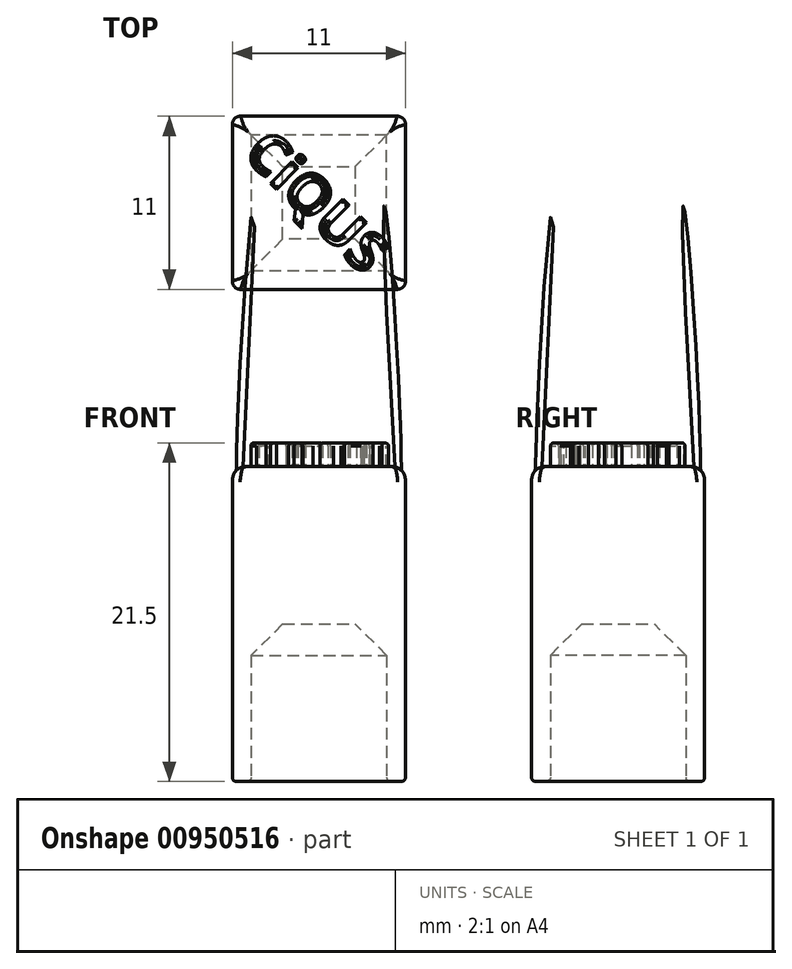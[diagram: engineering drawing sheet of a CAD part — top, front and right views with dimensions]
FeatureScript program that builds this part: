
annotation { "Feature Type Name" : "Feature", "Feature Type Description" : "" }
export const myFeature = defineFeature(function(context is Context, id is Id, definition is map)
    precondition{}
    {
        {
            var Q0;
            Q0=qCreatedBy(makeId("Top.planeOp"),FACE);
            var sketch = newSketch(context, id + "F0", { "sketchPlane" : qUnion([Q0])});
            skLineSegment(sketch, "E0.bottom", {"start": v(5.5, -5.5) * mm, "end": v(-5.5, -5.5) * mm});
            skLineSegment(sketch, "E0.top", {"start": v(5.5, 5.5) * mm, "end": v(-5.5, 5.5) * mm});
            skLineSegment(sketch, "E0.left", {"start": v(5.5, -5.5) * mm, "end": v(5.5, 5.5) * mm});
            skLineSegment(sketch, "E0.right", {"start": v(-5.5, -5.5) * mm, "end": v(-5.5, 5.5) * mm});
            skPoint(sketch, "E0.middle", {"position": v(0, 0) * mm});
            skSolve(sketch);
        }
        {
            var Q0;
            Q0=makeQuery(id+"F0.imprint","IMPRINT",FACE,{"disambiguationData":[TD([[makeQuery(id+"F0.imprint","IMPRINT",EDGE,{"derivedFrom":sQuery(id+"F0.wireOp",EDGE,"E0.bottom")}),-1.0]])]});
            extrude(context, id + "F1", {"entities" : qUnion([Q0]), "depth" : 20 * mm, "offsetDistance" : 25 * mm});
        }
        {
            var Q0;
            Q0=makeQuery(id+"F1.opExtrude","CAP_FACE",FACE,{"disambiguationData":[OSD([sQuery(id+"F0.wireOp",EDGE,"E0.bottom"),sQuery(id+"F0.wireOp",EDGE,"E0.top"),sQuery(id+"F0.wireOp",EDGE,"E0.left"),sQuery(id+"F0.wireOp",EDGE,"E0.right")])],"isStart":true});
            var sketch = newSketch(context, id + "F2", { "sketchPlane" : qUnion([Q0])});
            skLineSegment(sketch, "E1.bottom", {"start": v(-4.3, 4.3) * mm, "end": v(4.3, 4.3) * mm});
            skLineSegment(sketch, "E1.top", {"start": v(-4.3, -4.3) * mm, "end": v(4.3, -4.3) * mm});
            skLineSegment(sketch, "E1.left", {"start": v(-4.3, 4.3) * mm, "end": v(-4.3, -4.3) * mm});
            skLineSegment(sketch, "E1.right", {"start": v(4.3, 4.3) * mm, "end": v(4.3, -4.3) * mm});
            skPoint(sketch, "E1.middle", {"position": v(0, 0) * mm});
            skSolve(sketch);
        }
        {
            var Q0;
            Q0 = qSketchRegion(id + "F2", true);
            extrude(context, id + "F3", {"entities" : qUnion([Q0]), "operationType" : NewBodyOperationType.REMOVE, "oppositeDirection" : true, "depth" : 10 * mm, "offsetDistance" : 25 * mm});
        }
        {
            var Q0;
            Q0=makeQuery(id+"F1.opExtrude","CAP_FACE",FACE,{"disambiguationData":[OSD([sQuery(id+"F0.wireOp",EDGE,"E0.bottom"),sQuery(id+"F0.wireOp",EDGE,"E0.top"),sQuery(id+"F0.wireOp",EDGE,"E0.left"),sQuery(id+"F0.wireOp",EDGE,"E0.right")])],"isStart":true});
            fillet(context, id + "F4", {"entities" : qUnion([Q0]), "radius" : .25 * mm, "tangentPropagation" : true, "allowEdgeOverflow" : false});
        }
        {
            var Q0;
            Q0=makeQuery(id+"F3.boolean.opBoolean","COPY",FACE,{"derivedFrom":makeQuery(id+"F3.opExtrude","CAP_FACE",FACE,{"disambiguationData":[OSD([sQuery(id+"F2.wireOp",EDGE,"E1.bottom"),sQuery(id+"F2.wireOp",EDGE,"E1.top"),sQuery(id+"F2.wireOp",EDGE,"E1.left"),sQuery(id+"F2.wireOp",EDGE,"E1.right")])],"isStart":false})});
            chamfer(context, id + "F5", {"entities" : qUnion([Q0]), "width" : 2 * mm, "tangentPropagation" : true});
        }
        {
            var Q0;
            Q0=makeQuery(id+"F1.opExtrude","CAP_FACE",FACE,{"disambiguationData":[OSD([sQuery(id+"F0.wireOp",EDGE,"E0.bottom"),sQuery(id+"F0.wireOp",EDGE,"E0.top"),sQuery(id+"F0.wireOp",EDGE,"E0.left"),sQuery(id+"F0.wireOp",EDGE,"E0.right")])],"isStart":false});
            var sketch = newSketch(context, id + "F6", { "sketchPlane" : qUnion([Q0])});
            skText(sketch, "E2", { "text": "CiQUS", "fontName": "OpenSans-Bold.ttf"});
            const initialGuessF6  = {"E2": [-0.0055, -0.00258, 1, 0, 0.00258]};
            skSetInitialGuess(sketch, initialGuessF6);
            skSolve(sketch);
        }
        {
            var Q0;
            Q0 = qSketchRegion(id + "F6", true);
            extrude(context, id + "F7", {"entities" : qUnion([Q0]), "depth" : 1.5 * mm, "offsetDistance" : 25 * mm});
        }
        {
            var Q0;
            Q0=makeQuery(id+"F7.opExtrude","SWEPT_BODY",BODY,{"disambiguationData":[OSD([sQuery(id+"F6.wireOp",EDGE,"E2.sketch_text.stroke-0"),sQuery(id+"F6.wireOp",EDGE,"E2.sketch_text.stroke-1"),sQuery(id+"F6.wireOp",EDGE,"E2.sketch_text.stroke-2"),sQuery(id+"F6.wireOp",EDGE,"E2.sketch_text.stroke-3"),sQuery(id+"F6.wireOp",EDGE,"E2.sketch_text.stroke-4"),sQuery(id+"F6.wireOp",EDGE,"E2.sketch_text.stroke-5"),sQuery(id+"F6.wireOp",EDGE,"E2.sketch_text.stroke-6"),sQuery(id+"F6.wireOp",EDGE,"E2.sketch_text.stroke-7"),sQuery(id+"F6.wireOp",EDGE,"E2.sketch_text.stroke-8"),sQuery(id+"F6.wireOp",EDGE,"E2.sketch_text.stroke-9"),sQuery(id+"F6.wireOp",EDGE,"E2.sketch_text.stroke-10"),sQuery(id+"F6.wireOp",EDGE,"E2.sketch_text.stroke-11"),sQuery(id+"F6.wireOp",EDGE,"E2.sketch_text.stroke-12"),sQuery(id+"F6.wireOp",EDGE,"E2.sketch_text.stroke-13"),sQuery(id+"F6.wireOp",EDGE,"E2.sketch_text.stroke-14")])]});
            var Q1;
            Q1=makeQuery(id+"F7.opExtrude","SWEPT_BODY",BODY,{"disambiguationData":[OSD([sQuery(id+"F6.wireOp",EDGE,"E2.sketch_text.stroke-15"),sQuery(id+"F6.wireOp",EDGE,"E2.sketch_text.stroke-16"),sQuery(id+"F6.wireOp",EDGE,"E2.sketch_text.stroke-17"),sQuery(id+"F6.wireOp",EDGE,"E2.sketch_text.stroke-18"),sQuery(id+"F6.wireOp",EDGE,"E2.sketch_text.stroke-19")])]});
            var Q2;
            Q2=makeQuery(id+"F7.opExtrude","SWEPT_BODY",BODY,{"disambiguationData":[OSD([sQuery(id+"F6.wireOp",EDGE,"E2.sketch_text.stroke-20"),sQuery(id+"F6.wireOp",EDGE,"E2.sketch_text.stroke-21"),sQuery(id+"F6.wireOp",EDGE,"E2.sketch_text.stroke-22"),sQuery(id+"F6.wireOp",EDGE,"E2.sketch_text.stroke-23")])]});
            var Q3;
            Q3=makeQuery(id+"F7.opExtrude","SWEPT_BODY",BODY,{"disambiguationData":[OSD([sQuery(id+"F6.wireOp",EDGE,"E2.sketch_text.stroke-24"),sQuery(id+"F6.wireOp",EDGE,"E2.sketch_text.stroke-25"),sQuery(id+"F6.wireOp",EDGE,"E2.sketch_text.stroke-26"),sQuery(id+"F6.wireOp",EDGE,"E2.sketch_text.stroke-27"),sQuery(id+"F6.wireOp",EDGE,"E2.sketch_text.stroke-28"),sQuery(id+"F6.wireOp",EDGE,"E2.sketch_text.stroke-29"),sQuery(id+"F6.wireOp",EDGE,"E2.sketch_text.stroke-30"),sQuery(id+"F6.wireOp",EDGE,"E2.sketch_text.stroke-31"),sQuery(id+"F6.wireOp",EDGE,"E2.sketch_text.stroke-32"),sQuery(id+"F6.wireOp",EDGE,"E2.sketch_text.stroke-33"),sQuery(id+"F6.wireOp",EDGE,"E2.sketch_text.stroke-34"),sQuery(id+"F6.wireOp",EDGE,"E2.sketch_text.stroke-35"),sQuery(id+"F6.wireOp",EDGE,"E2.sketch_text.stroke-36"),sQuery(id+"F6.wireOp",EDGE,"E2.sketch_text.stroke-37"),sQuery(id+"F6.wireOp",EDGE,"E2.sketch_text.stroke-38"),sQuery(id+"F6.wireOp",EDGE,"E2.sketch_text.stroke-39"),sQuery(id+"F6.wireOp",EDGE,"E2.sketch_text.stroke-40"),sQuery(id+"F6.wireOp",EDGE,"E2.sketch_text.stroke-41")])]});
            var Q4;
            Q4=makeQuery(id+"F7.opExtrude","SWEPT_BODY",BODY,{"disambiguationData":[OSD([sQuery(id+"F6.wireOp",EDGE,"E2.sketch_text.stroke-42"),sQuery(id+"F6.wireOp",EDGE,"E2.sketch_text.stroke-43"),sQuery(id+"F6.wireOp",EDGE,"E2.sketch_text.stroke-44"),sQuery(id+"F6.wireOp",EDGE,"E2.sketch_text.stroke-45"),sQuery(id+"F6.wireOp",EDGE,"E2.sketch_text.stroke-46"),sQuery(id+"F6.wireOp",EDGE,"E2.sketch_text.stroke-47"),sQuery(id+"F6.wireOp",EDGE,"E2.sketch_text.stroke-48"),sQuery(id+"F6.wireOp",EDGE,"E2.sketch_text.stroke-49"),sQuery(id+"F6.wireOp",EDGE,"E2.sketch_text.stroke-50"),sQuery(id+"F6.wireOp",EDGE,"E2.sketch_text.stroke-51"),sQuery(id+"F6.wireOp",EDGE,"E2.sketch_text.stroke-52"),sQuery(id+"F6.wireOp",EDGE,"E2.sketch_text.stroke-53"),sQuery(id+"F6.wireOp",EDGE,"E2.sketch_text.stroke-54"),sQuery(id+"F6.wireOp",EDGE,"E2.sketch_text.stroke-55"),sQuery(id+"F6.wireOp",EDGE,"E2.sketch_text.stroke-56")])]});
            var Q5;
            Q5=makeQuery(id+"F7.opExtrude","SWEPT_BODY",BODY,{"disambiguationData":[OSD([sQuery(id+"F6.wireOp",EDGE,"E2.sketch_text.stroke-57"),sQuery(id+"F6.wireOp",EDGE,"E2.sketch_text.stroke-58"),sQuery(id+"F6.wireOp",EDGE,"E2.sketch_text.stroke-59"),sQuery(id+"F6.wireOp",EDGE,"E2.sketch_text.stroke-60"),sQuery(id+"F6.wireOp",EDGE,"E2.sketch_text.stroke-61"),sQuery(id+"F6.wireOp",EDGE,"E2.sketch_text.stroke-62"),sQuery(id+"F6.wireOp",EDGE,"E2.sketch_text.stroke-63"),sQuery(id+"F6.wireOp",EDGE,"E2.sketch_text.stroke-64"),sQuery(id+"F6.wireOp",EDGE,"E2.sketch_text.stroke-65"),sQuery(id+"F6.wireOp",EDGE,"E2.sketch_text.stroke-66"),sQuery(id+"F6.wireOp",EDGE,"E2.sketch_text.stroke-67"),sQuery(id+"F6.wireOp",EDGE,"E2.sketch_text.stroke-68"),sQuery(id+"F6.wireOp",EDGE,"E2.sketch_text.stroke-69"),sQuery(id+"F6.wireOp",EDGE,"E2.sketch_text.stroke-70"),sQuery(id+"F6.wireOp",EDGE,"E2.sketch_text.stroke-71"),sQuery(id+"F6.wireOp",EDGE,"E2.sketch_text.stroke-72"),sQuery(id+"F6.wireOp",EDGE,"E2.sketch_text.stroke-73"),sQuery(id+"F6.wireOp",EDGE,"E2.sketch_text.stroke-74"),sQuery(id+"F6.wireOp",EDGE,"E2.sketch_text.stroke-75"),sQuery(id+"F6.wireOp",EDGE,"E2.sketch_text.stroke-76"),sQuery(id+"F6.wireOp",EDGE,"E2.sketch_text.stroke-77"),sQuery(id+"F6.wireOp",EDGE,"E2.sketch_text.stroke-78"),sQuery(id+"F6.wireOp",EDGE,"E2.sketch_text.stroke-79"),sQuery(id+"F6.wireOp",EDGE,"E2.sketch_text.stroke-80"),sQuery(id+"F6.wireOp",EDGE,"E2.sketch_text.stroke-81"),sQuery(id+"F6.wireOp",EDGE,"E2.sketch_text.stroke-82"),sQuery(id+"F6.wireOp",EDGE,"E2.sketch_text.stroke-83"),sQuery(id+"F6.wireOp",EDGE,"E2.sketch_text.stroke-84")])]});
            var Q6;
            Q6=makeQuery(id+"F1.opExtrude","SWEPT_EDGE",EDGE,{"disambiguationData":[OSD([sQuery(id+"F0.wireOp",EDGE,"E0.bottom"),sQuery(id+"F0.wireOp",EDGE,"E0.left")])]});
            transform(context, id + "F8", {"entities" : qUnion([Q0, Q1, Q2, Q3, Q4, Q5]), "transformType" : TransformType.ROTATION, "transformAxis" : qUnion([Q6]), "angle" : 45 * degree, "makeCopy" : false});
        }
        {
            var Q0;
            Q0=makeQuery(id+"F7.opExtrude","SWEPT_BODY",BODY,{"disambiguationData":[OSD([sQuery(id+"F6.wireOp",EDGE,"E2.sketch_text.stroke-0"),sQuery(id+"F6.wireOp",EDGE,"E2.sketch_text.stroke-1"),sQuery(id+"F6.wireOp",EDGE,"E2.sketch_text.stroke-2"),sQuery(id+"F6.wireOp",EDGE,"E2.sketch_text.stroke-3"),sQuery(id+"F6.wireOp",EDGE,"E2.sketch_text.stroke-4"),sQuery(id+"F6.wireOp",EDGE,"E2.sketch_text.stroke-5"),sQuery(id+"F6.wireOp",EDGE,"E2.sketch_text.stroke-6"),sQuery(id+"F6.wireOp",EDGE,"E2.sketch_text.stroke-7"),sQuery(id+"F6.wireOp",EDGE,"E2.sketch_text.stroke-8"),sQuery(id+"F6.wireOp",EDGE,"E2.sketch_text.stroke-9"),sQuery(id+"F6.wireOp",EDGE,"E2.sketch_text.stroke-10"),sQuery(id+"F6.wireOp",EDGE,"E2.sketch_text.stroke-11"),sQuery(id+"F6.wireOp",EDGE,"E2.sketch_text.stroke-12"),sQuery(id+"F6.wireOp",EDGE,"E2.sketch_text.stroke-13"),sQuery(id+"F6.wireOp",EDGE,"E2.sketch_text.stroke-14")])]});
            var Q1;
            Q1=makeQuery(id+"F7.opExtrude","SWEPT_BODY",BODY,{"disambiguationData":[OSD([sQuery(id+"F6.wireOp",EDGE,"E2.sketch_text.stroke-15"),sQuery(id+"F6.wireOp",EDGE,"E2.sketch_text.stroke-16"),sQuery(id+"F6.wireOp",EDGE,"E2.sketch_text.stroke-17"),sQuery(id+"F6.wireOp",EDGE,"E2.sketch_text.stroke-18"),sQuery(id+"F6.wireOp",EDGE,"E2.sketch_text.stroke-19")])]});
            var Q2;
            Q2=makeQuery(id+"F7.opExtrude","SWEPT_BODY",BODY,{"disambiguationData":[OSD([sQuery(id+"F6.wireOp",EDGE,"E2.sketch_text.stroke-20"),sQuery(id+"F6.wireOp",EDGE,"E2.sketch_text.stroke-21"),sQuery(id+"F6.wireOp",EDGE,"E2.sketch_text.stroke-22"),sQuery(id+"F6.wireOp",EDGE,"E2.sketch_text.stroke-23")])]});
            var Q3;
            Q3=makeQuery(id+"F7.opExtrude","SWEPT_BODY",BODY,{"disambiguationData":[OSD([sQuery(id+"F6.wireOp",EDGE,"E2.sketch_text.stroke-24"),sQuery(id+"F6.wireOp",EDGE,"E2.sketch_text.stroke-25"),sQuery(id+"F6.wireOp",EDGE,"E2.sketch_text.stroke-26"),sQuery(id+"F6.wireOp",EDGE,"E2.sketch_text.stroke-27"),sQuery(id+"F6.wireOp",EDGE,"E2.sketch_text.stroke-28"),sQuery(id+"F6.wireOp",EDGE,"E2.sketch_text.stroke-29"),sQuery(id+"F6.wireOp",EDGE,"E2.sketch_text.stroke-30"),sQuery(id+"F6.wireOp",EDGE,"E2.sketch_text.stroke-31"),sQuery(id+"F6.wireOp",EDGE,"E2.sketch_text.stroke-32"),sQuery(id+"F6.wireOp",EDGE,"E2.sketch_text.stroke-33"),sQuery(id+"F6.wireOp",EDGE,"E2.sketch_text.stroke-34"),sQuery(id+"F6.wireOp",EDGE,"E2.sketch_text.stroke-35"),sQuery(id+"F6.wireOp",EDGE,"E2.sketch_text.stroke-36"),sQuery(id+"F6.wireOp",EDGE,"E2.sketch_text.stroke-37"),sQuery(id+"F6.wireOp",EDGE,"E2.sketch_text.stroke-38"),sQuery(id+"F6.wireOp",EDGE,"E2.sketch_text.stroke-39"),sQuery(id+"F6.wireOp",EDGE,"E2.sketch_text.stroke-40"),sQuery(id+"F6.wireOp",EDGE,"E2.sketch_text.stroke-41")])]});
            var Q4;
            Q4=makeQuery(id+"F7.opExtrude","SWEPT_BODY",BODY,{"disambiguationData":[OSD([sQuery(id+"F6.wireOp",EDGE,"E2.sketch_text.stroke-42"),sQuery(id+"F6.wireOp",EDGE,"E2.sketch_text.stroke-43"),sQuery(id+"F6.wireOp",EDGE,"E2.sketch_text.stroke-44"),sQuery(id+"F6.wireOp",EDGE,"E2.sketch_text.stroke-45"),sQuery(id+"F6.wireOp",EDGE,"E2.sketch_text.stroke-46"),sQuery(id+"F6.wireOp",EDGE,"E2.sketch_text.stroke-47"),sQuery(id+"F6.wireOp",EDGE,"E2.sketch_text.stroke-48"),sQuery(id+"F6.wireOp",EDGE,"E2.sketch_text.stroke-49"),sQuery(id+"F6.wireOp",EDGE,"E2.sketch_text.stroke-50"),sQuery(id+"F6.wireOp",EDGE,"E2.sketch_text.stroke-51"),sQuery(id+"F6.wireOp",EDGE,"E2.sketch_text.stroke-52"),sQuery(id+"F6.wireOp",EDGE,"E2.sketch_text.stroke-53"),sQuery(id+"F6.wireOp",EDGE,"E2.sketch_text.stroke-54"),sQuery(id+"F6.wireOp",EDGE,"E2.sketch_text.stroke-55"),sQuery(id+"F6.wireOp",EDGE,"E2.sketch_text.stroke-56")])]});
            var Q5;
            Q5=makeQuery(id+"F7.opExtrude","SWEPT_BODY",BODY,{"disambiguationData":[OSD([sQuery(id+"F6.wireOp",EDGE,"E2.sketch_text.stroke-57"),sQuery(id+"F6.wireOp",EDGE,"E2.sketch_text.stroke-58"),sQuery(id+"F6.wireOp",EDGE,"E2.sketch_text.stroke-59"),sQuery(id+"F6.wireOp",EDGE,"E2.sketch_text.stroke-60"),sQuery(id+"F6.wireOp",EDGE,"E2.sketch_text.stroke-61"),sQuery(id+"F6.wireOp",EDGE,"E2.sketch_text.stroke-62"),sQuery(id+"F6.wireOp",EDGE,"E2.sketch_text.stroke-63"),sQuery(id+"F6.wireOp",EDGE,"E2.sketch_text.stroke-64"),sQuery(id+"F6.wireOp",EDGE,"E2.sketch_text.stroke-65"),sQuery(id+"F6.wireOp",EDGE,"E2.sketch_text.stroke-66"),sQuery(id+"F6.wireOp",EDGE,"E2.sketch_text.stroke-67"),sQuery(id+"F6.wireOp",EDGE,"E2.sketch_text.stroke-68"),sQuery(id+"F6.wireOp",EDGE,"E2.sketch_text.stroke-69"),sQuery(id+"F6.wireOp",EDGE,"E2.sketch_text.stroke-70"),sQuery(id+"F6.wireOp",EDGE,"E2.sketch_text.stroke-71"),sQuery(id+"F6.wireOp",EDGE,"E2.sketch_text.stroke-72"),sQuery(id+"F6.wireOp",EDGE,"E2.sketch_text.stroke-73"),sQuery(id+"F6.wireOp",EDGE,"E2.sketch_text.stroke-74"),sQuery(id+"F6.wireOp",EDGE,"E2.sketch_text.stroke-75"),sQuery(id+"F6.wireOp",EDGE,"E2.sketch_text.stroke-76"),sQuery(id+"F6.wireOp",EDGE,"E2.sketch_text.stroke-77"),sQuery(id+"F6.wireOp",EDGE,"E2.sketch_text.stroke-78"),sQuery(id+"F6.wireOp",EDGE,"E2.sketch_text.stroke-79"),sQuery(id+"F6.wireOp",EDGE,"E2.sketch_text.stroke-80"),sQuery(id+"F6.wireOp",EDGE,"E2.sketch_text.stroke-81"),sQuery(id+"F6.wireOp",EDGE,"E2.sketch_text.stroke-82"),sQuery(id+"F6.wireOp",EDGE,"E2.sketch_text.stroke-83"),sQuery(id+"F6.wireOp",EDGE,"E2.sketch_text.stroke-84")])]});
            transform(context, id + "F9", {"entities" : qUnion([Q0, Q1, Q2, Q3, Q4, Q5]), "transformType" : TransformType.TRANSLATION_3D, "dx" : -4.68 * mm, "dy" : -1.3 * mm, "dz" : 0 * mm, "makeCopy" : false});
        }
        {
            var Q0;
            Q0=makeQuery(id+"F1.opExtrude","CAP_FACE",FACE,{"disambiguationData":[OSD([sQuery(id+"F0.wireOp",EDGE,"E0.bottom"),sQuery(id+"F0.wireOp",EDGE,"E0.top"),sQuery(id+"F0.wireOp",EDGE,"E0.left"),sQuery(id+"F0.wireOp",EDGE,"E0.right")])],"isStart":false});
            fillet(context, id + "F10", {"entities" : qUnion([Q0]), "radius" : 1 * mm, "tangentPropagation" : true, "rho" : 0.5, "crossSection" : FilletCrossSection.CONIC, "allowEdgeOverflow" : false});
        }
        {
            var Q0;
            Q0=makeQuery(id+"F1.opExtrude","SWEPT_EDGE",EDGE,{"disambiguationData":[OSD([sQuery(id+"F0.wireOp",EDGE,"E0.bottom"),sQuery(id+"F0.wireOp",EDGE,"E0.left")])]});
            var Q1;
            Q1=makeQuery(id+"F1.opExtrude","SWEPT_EDGE",EDGE,{"disambiguationData":[OSD([sQuery(id+"F0.wireOp",EDGE,"E0.top"),sQuery(id+"F0.wireOp",EDGE,"E0.left")])]});
            var Q2;
            Q2=makeQuery(id+"F1.opExtrude","SWEPT_EDGE",EDGE,{"disambiguationData":[OSD([sQuery(id+"F0.wireOp",EDGE,"E0.bottom"),sQuery(id+"F0.wireOp",EDGE,"E0.right")])]});
            var Q3;
            Q3=makeQuery(id+"F1.opExtrude","SWEPT_EDGE",EDGE,{"disambiguationData":[OSD([sQuery(id+"F0.wireOp",EDGE,"E0.top"),sQuery(id+"F0.wireOp",EDGE,"E0.right")])]});
            fillet(context, id + "F11", {"entities" : qUnion([Q0, Q1, Q2, Q3]), "radius" : .5 * mm, "tangentPropagation" : true, "allowEdgeOverflow" : false});
        }
        {
            var Q0;
            Q0=makeQuery(id+"F7.opExtrude","CAP_FACE",FACE,{"disambiguationData":[OSD([sQuery(id+"F6.wireOp",EDGE,"E2.sketch_text.stroke-0"),sQuery(id+"F6.wireOp",EDGE,"E2.sketch_text.stroke-1"),sQuery(id+"F6.wireOp",EDGE,"E2.sketch_text.stroke-2"),sQuery(id+"F6.wireOp",EDGE,"E2.sketch_text.stroke-3"),sQuery(id+"F6.wireOp",EDGE,"E2.sketch_text.stroke-4"),sQuery(id+"F6.wireOp",EDGE,"E2.sketch_text.stroke-5"),sQuery(id+"F6.wireOp",EDGE,"E2.sketch_text.stroke-6"),sQuery(id+"F6.wireOp",EDGE,"E2.sketch_text.stroke-7"),sQuery(id+"F6.wireOp",EDGE,"E2.sketch_text.stroke-8"),sQuery(id+"F6.wireOp",EDGE,"E2.sketch_text.stroke-9"),sQuery(id+"F6.wireOp",EDGE,"E2.sketch_text.stroke-10"),sQuery(id+"F6.wireOp",EDGE,"E2.sketch_text.stroke-11"),sQuery(id+"F6.wireOp",EDGE,"E2.sketch_text.stroke-12"),sQuery(id+"F6.wireOp",EDGE,"E2.sketch_text.stroke-13"),sQuery(id+"F6.wireOp",EDGE,"E2.sketch_text.stroke-14")])],"isStart":false});
            var Q1;
            Q1=makeQuery(id+"F7.opExtrude","CAP_FACE",FACE,{"disambiguationData":[OSD([sQuery(id+"F6.wireOp",EDGE,"E2.sketch_text.stroke-20"),sQuery(id+"F6.wireOp",EDGE,"E2.sketch_text.stroke-21"),sQuery(id+"F6.wireOp",EDGE,"E2.sketch_text.stroke-22"),sQuery(id+"F6.wireOp",EDGE,"E2.sketch_text.stroke-23")])],"isStart":false});
            var Q2;
            Q2=makeQuery(id+"F7.opExtrude","CAP_FACE",FACE,{"disambiguationData":[OSD([sQuery(id+"F6.wireOp",EDGE,"E2.sketch_text.stroke-15"),sQuery(id+"F6.wireOp",EDGE,"E2.sketch_text.stroke-16"),sQuery(id+"F6.wireOp",EDGE,"E2.sketch_text.stroke-17"),sQuery(id+"F6.wireOp",EDGE,"E2.sketch_text.stroke-18"),sQuery(id+"F6.wireOp",EDGE,"E2.sketch_text.stroke-19")])],"isStart":false});
            var Q3;
            Q3=makeQuery(id+"F7.opExtrude","CAP_FACE",FACE,{"disambiguationData":[OSD([sQuery(id+"F6.wireOp",EDGE,"E2.sketch_text.stroke-24"),sQuery(id+"F6.wireOp",EDGE,"E2.sketch_text.stroke-25"),sQuery(id+"F6.wireOp",EDGE,"E2.sketch_text.stroke-26"),sQuery(id+"F6.wireOp",EDGE,"E2.sketch_text.stroke-27"),sQuery(id+"F6.wireOp",EDGE,"E2.sketch_text.stroke-28"),sQuery(id+"F6.wireOp",EDGE,"E2.sketch_text.stroke-29"),sQuery(id+"F6.wireOp",EDGE,"E2.sketch_text.stroke-30"),sQuery(id+"F6.wireOp",EDGE,"E2.sketch_text.stroke-31"),sQuery(id+"F6.wireOp",EDGE,"E2.sketch_text.stroke-32"),sQuery(id+"F6.wireOp",EDGE,"E2.sketch_text.stroke-33"),sQuery(id+"F6.wireOp",EDGE,"E2.sketch_text.stroke-34"),sQuery(id+"F6.wireOp",EDGE,"E2.sketch_text.stroke-35"),sQuery(id+"F6.wireOp",EDGE,"E2.sketch_text.stroke-36"),sQuery(id+"F6.wireOp",EDGE,"E2.sketch_text.stroke-37"),sQuery(id+"F6.wireOp",EDGE,"E2.sketch_text.stroke-38"),sQuery(id+"F6.wireOp",EDGE,"E2.sketch_text.stroke-39"),sQuery(id+"F6.wireOp",EDGE,"E2.sketch_text.stroke-40"),sQuery(id+"F6.wireOp",EDGE,"E2.sketch_text.stroke-41")])],"isStart":false});
            var Q4;
            Q4=makeQuery(id+"F7.opExtrude","CAP_FACE",FACE,{"disambiguationData":[OSD([sQuery(id+"F6.wireOp",EDGE,"E2.sketch_text.stroke-57"),sQuery(id+"F6.wireOp",EDGE,"E2.sketch_text.stroke-58"),sQuery(id+"F6.wireOp",EDGE,"E2.sketch_text.stroke-59"),sQuery(id+"F6.wireOp",EDGE,"E2.sketch_text.stroke-60"),sQuery(id+"F6.wireOp",EDGE,"E2.sketch_text.stroke-61"),sQuery(id+"F6.wireOp",EDGE,"E2.sketch_text.stroke-62"),sQuery(id+"F6.wireOp",EDGE,"E2.sketch_text.stroke-63"),sQuery(id+"F6.wireOp",EDGE,"E2.sketch_text.stroke-64"),sQuery(id+"F6.wireOp",EDGE,"E2.sketch_text.stroke-65"),sQuery(id+"F6.wireOp",EDGE,"E2.sketch_text.stroke-66"),sQuery(id+"F6.wireOp",EDGE,"E2.sketch_text.stroke-67"),sQuery(id+"F6.wireOp",EDGE,"E2.sketch_text.stroke-68"),sQuery(id+"F6.wireOp",EDGE,"E2.sketch_text.stroke-69"),sQuery(id+"F6.wireOp",EDGE,"E2.sketch_text.stroke-70"),sQuery(id+"F6.wireOp",EDGE,"E2.sketch_text.stroke-71"),sQuery(id+"F6.wireOp",EDGE,"E2.sketch_text.stroke-72"),sQuery(id+"F6.wireOp",EDGE,"E2.sketch_text.stroke-73"),sQuery(id+"F6.wireOp",EDGE,"E2.sketch_text.stroke-74"),sQuery(id+"F6.wireOp",EDGE,"E2.sketch_text.stroke-75"),sQuery(id+"F6.wireOp",EDGE,"E2.sketch_text.stroke-76"),sQuery(id+"F6.wireOp",EDGE,"E2.sketch_text.stroke-77"),sQuery(id+"F6.wireOp",EDGE,"E2.sketch_text.stroke-78"),sQuery(id+"F6.wireOp",EDGE,"E2.sketch_text.stroke-79"),sQuery(id+"F6.wireOp",EDGE,"E2.sketch_text.stroke-80"),sQuery(id+"F6.wireOp",EDGE,"E2.sketch_text.stroke-81"),sQuery(id+"F6.wireOp",EDGE,"E2.sketch_text.stroke-82"),sQuery(id+"F6.wireOp",EDGE,"E2.sketch_text.stroke-83"),sQuery(id+"F6.wireOp",EDGE,"E2.sketch_text.stroke-84")])],"isStart":false});
            var Q5;
            Q5=makeQuery(id+"F7.opExtrude","CAP_FACE",FACE,{"disambiguationData":[OSD([sQuery(id+"F6.wireOp",EDGE,"E2.sketch_text.stroke-42"),sQuery(id+"F6.wireOp",EDGE,"E2.sketch_text.stroke-43"),sQuery(id+"F6.wireOp",EDGE,"E2.sketch_text.stroke-44"),sQuery(id+"F6.wireOp",EDGE,"E2.sketch_text.stroke-45"),sQuery(id+"F6.wireOp",EDGE,"E2.sketch_text.stroke-46"),sQuery(id+"F6.wireOp",EDGE,"E2.sketch_text.stroke-47"),sQuery(id+"F6.wireOp",EDGE,"E2.sketch_text.stroke-48"),sQuery(id+"F6.wireOp",EDGE,"E2.sketch_text.stroke-49"),sQuery(id+"F6.wireOp",EDGE,"E2.sketch_text.stroke-50"),sQuery(id+"F6.wireOp",EDGE,"E2.sketch_text.stroke-51"),sQuery(id+"F6.wireOp",EDGE,"E2.sketch_text.stroke-52"),sQuery(id+"F6.wireOp",EDGE,"E2.sketch_text.stroke-53"),sQuery(id+"F6.wireOp",EDGE,"E2.sketch_text.stroke-54"),sQuery(id+"F6.wireOp",EDGE,"E2.sketch_text.stroke-55"),sQuery(id+"F6.wireOp",EDGE,"E2.sketch_text.stroke-56")])],"isStart":false});
            fillet(context, id + "F12", {"entities" : qUnion([Q0, Q1, Q2, Q3, Q4, Q5]), "radius" : .2 * mm, "tangentPropagation" : true, "allowEdgeOverflow" : false});
        }
    });
